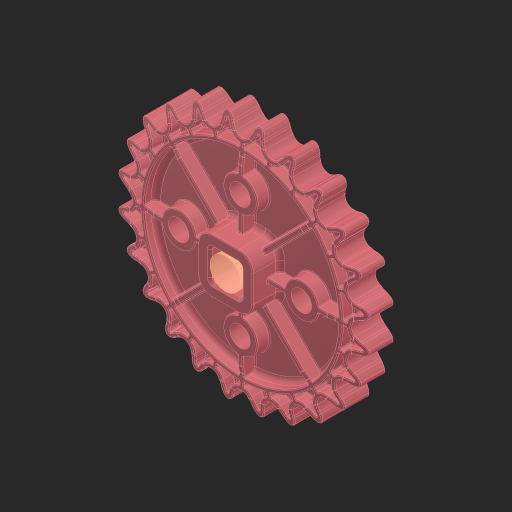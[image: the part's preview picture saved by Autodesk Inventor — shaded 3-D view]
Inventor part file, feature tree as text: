
AUTODESK INVENTOR PART (.ipt)
format: ipt  version: 2023 (Build 270158000, 158)  size: 7,190,016 bytes
history: native  units: in
note: dims shown in document units (in); Inventor stores cm internally (conversion verified against a paired STEP export)
features: sketch x1, other x1, mirror x1, extrude x1
ambient origin geometry x8: Origin, YZ Plane, XZ Plane, XY Plane, X Axis, Y Axis, Z Axis, Center Point
bodies: Solid1 (feature_tree)
feature tree (4):
  sketch  "Sketch1"  dims[d0=0.25in d1=0.3937in d2=0.0in]
  other  "Srf1"
  mirror  "Mirror6"
  extrude  "ExtrusionSrf1"  Depth=0.3937in TaperAngle=0.0deg
